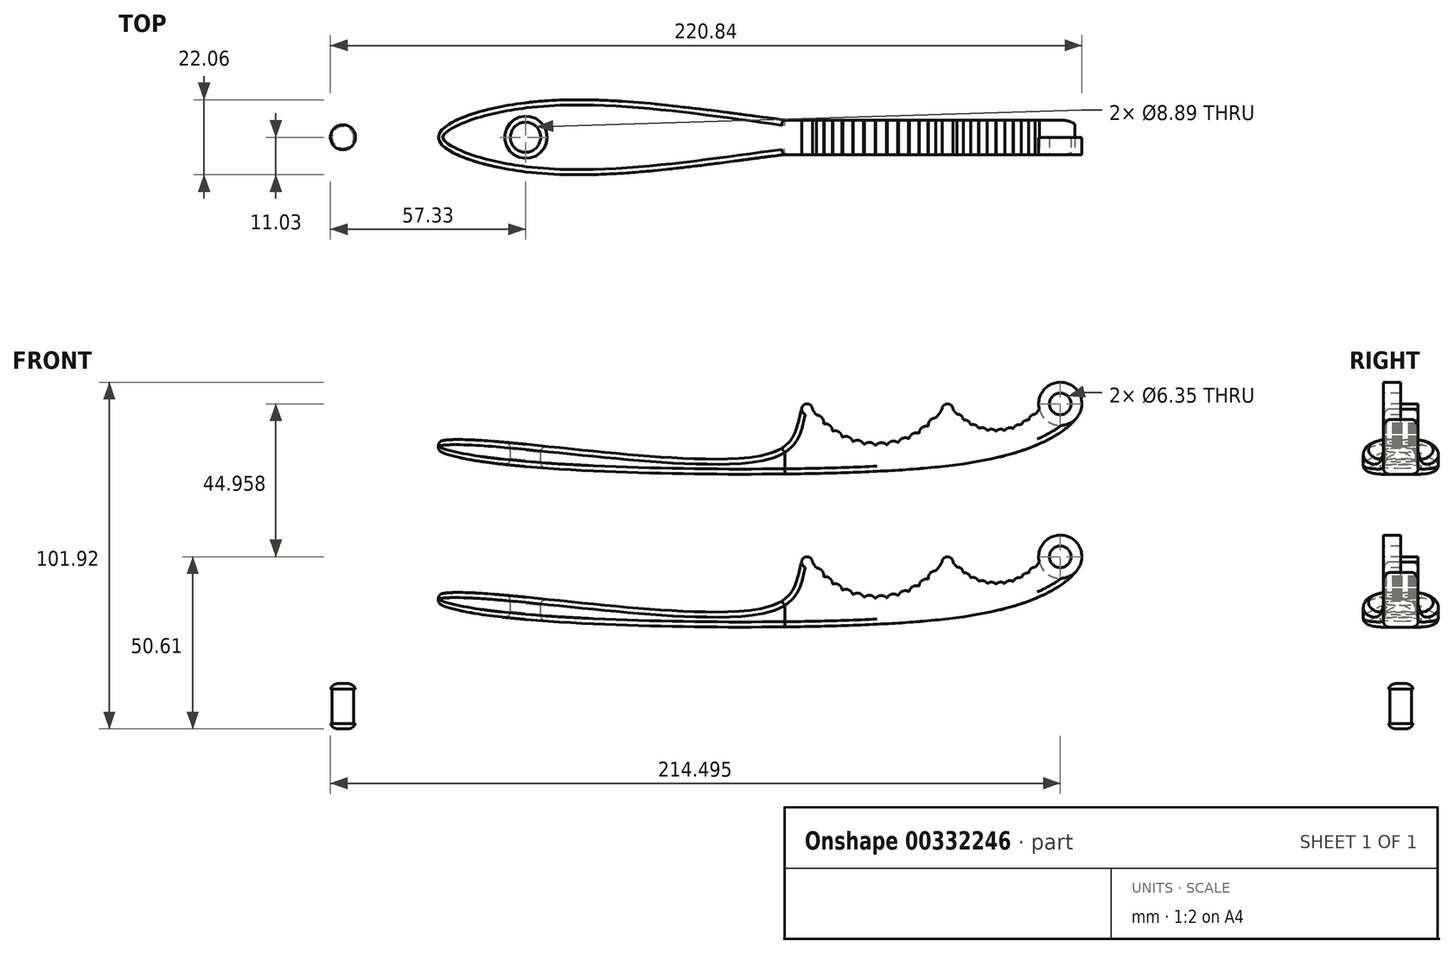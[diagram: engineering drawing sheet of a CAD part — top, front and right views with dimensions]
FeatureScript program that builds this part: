
annotation { "Feature Type Name" : "Feature", "Feature Type Description" : "" }
export const myFeature = defineFeature(function(context is Context, id is Id, definition is map)
    precondition{}
    {
        {
            var Q0;
            Q0=qCreatedBy(makeId("Front.planeOp"),FACE);
            var sketch = newSketch(context, id + "F0", { "sketchPlane" : qUnion([Q0])});
            skLineSegment(sketch, "E0", {"start": v(-75.4, 0) * mm, "end": v(106.36, 0) * mm});
            skCircle(sketch, "E1", {"center": v(106.36, 0) * mm, "radius": 3.18 * mm});
            skCircle(sketch, "E2", {"center": v(106.36, 0) * mm, "radius": 6.35 * mm});
            skLineSegment(sketch, "E3", {"start": v(100.01, 0) * mm, "end": v(77.68, 0) * mm});
            skLineSegment(sketch, "E4", {"start": v(77.68, 0) * mm, "end": v(88.85, 0) * mm});
            skLineSegment(sketch, "E5", {"start": v(-75.4, 0) * mm, "end": v(-75.4, -1.59) * mm});
            skLineSegment(sketch, "E6", {"start": v(106.36, 0) * mm, "end": v(106.36, -1.59) * mm});
            skLineSegment(sketch, "E7", {"start": v(-75.4, -1.59) * mm, "end": v(106.36, -1.59) * mm});
            skArc(sketch, "E8", {"start": v(74.82, -1.59) * mm, "mid": v(73.23, 0) * mm, "end": v(71.64, -1.59) * mm});
            skLineSegment(sketch, "E9", {"start": v(71.64, -1.59) * mm, "end": v(33.54, -1.59) * mm});
            skArc(sketch, "E10", {"start": v(33.54, -1.59) * mm, "mid": v(52.6, -12.22) * mm, "end": v(71.64, -1.59) * mm});
            skArc(sketch, "E11", {"start": v(74.82, -1.59) * mm, "mid": v(87.52, -8.07) * mm, "end": v(100.22, -1.59) * mm});
            skArc(sketch, "E12", {"start": v(33.54, -1.59) * mm, "mid": v(31.95, 0) * mm, "end": v(30.37, -1.59) * mm});
            skLineSegment(sketch, "E13", {"start": v(106.36, 0) * mm, "end": v(112.71, 0) * mm});
            skLineSegment(sketch, "E14", {"start": v(52.6, -12.22) * mm, "end": v(52.6, -19.84) * mm});
            skPoint(sketch, "E15.endSnap0", {"position": v(87.52, -8.07) * mm});
            skLineSegment(sketch, "E16", {"start": v(31.95, -1.59) * mm, "end": v(-76.4, -1.59) * mm});
            skLineSegment(sketch, "E17", {"start": v(106.36, -1.59) * mm, "end": v(106.36, -6.35) * mm});
            skLineSegment(sketch, "E18", {"start": v(106.36, 0) * mm, "end": v(110.68, -4.66) * mm});
            skLineSegment(sketch, "E19", {"start": v(100.22, -1.59) * mm, "end": v(100.22, -11.75) * mm});
            skFitSpline(sketch, "E20", {"points": [v(112.71, 0) * mm, v(110.68, -4.66) * mm, v(100.22, -11.75) * mm, v(52.6, -19.84) * mm, v(-76.4, -13.65) * mm, v(-76.4, -11.11) * mm, v(21.94, -14.29) * mm, v(30.37, -1.59) * mm], "startDerivative": vector(-21.93, -81.83) * mm, "endDerivative": vector(45.44, 125.18) * mm});
            skLineSegment(sketch, "E21", {"start": v(52.6, 10.16) * mm, "end": v(52.6, 10.16) * mm});
            skPoint(sketch, "E22.center", {"position": v(0, 0) * mm});
            skArc(sketch, "E23", {"start": v(69.79, -4.16) * mm, "mid": v(68.16, -4.8) * mm, "end": v(67.59, -6.45) * mm});
            skArc(sketch, "E24.1.0", {"start": v(67.44, -6.58) * mm, "mid": v(65.74, -6.97) * mm, "end": v(64.92, -8.52) * mm});
            skArc(sketch, "E24.2.0", {"start": v(64.76, -8.62) * mm, "mid": v(63.02, -8.75) * mm, "end": v(61.98, -10.16) * mm});
            skArc(sketch, "E24.3.0", {"start": v(61.8, -10.24) * mm, "mid": v(60.06, -10.1) * mm, "end": v(58.82, -11.34) * mm});
            skArc(sketch, "E24.4.0", {"start": v(58.63, -11.4) * mm, "mid": v(56.93, -11) * mm, "end": v(55.52, -12.03) * mm});
            skArc(sketch, "E24.5.0", {"start": v(55.33, -12.05) * mm, "mid": v(53.7, -11.4) * mm, "end": v(52.16, -12.22) * mm});
            skArc(sketch, "E24.6.0", {"start": v(51.96, -12.21) * mm, "mid": v(50.45, -11.33) * mm, "end": v(48.8, -11.9) * mm});
            skArc(sketch, "E24.7.0", {"start": v(48.6, -11.86) * mm, "mid": v(47.25, -10.77) * mm, "end": v(45.53, -11.08) * mm});
            skArc(sketch, "E24.8.0", {"start": v(45.35, -11.02) * mm, "mid": v(44.17, -9.73) * mm, "end": v(42.42, -9.78) * mm});
            skArc(sketch, "E24.9.0", {"start": v(42.25, -9.69) * mm, "mid": v(41.28, -8.24) * mm, "end": v(39.54, -8.02) * mm});
            skArc(sketch, "E24.10.0", {"start": v(39.39, -7.9) * mm, "mid": v(38.64, -6.33) * mm, "end": v(36.96, -5.86) * mm});
            skArc(sketch, "E24.11.0", {"start": v(36.82, -5.72) * mm, "mid": v(36.33, -4.05) * mm, "end": v(34.73, -3.33) * mm});
            skLineSegment(sketch, "E24.anchor1", {"start": v(52.6, 10.16) * mm, "end": v(67.59, -6.45) * mm, "construction": true});
            skLineSegment(sketch, "E24.anchor2", {"start": v(52.6, 10.16) * mm, "end": v(34.73, -3.33) * mm, "construction": true});
            skArc(sketch, "E25", {"start": v(98.99, -3.08) * mm, "mid": v(97.71, -3.56) * mm, "end": v(97.11, -4.79) * mm});
            skArc(sketch, "E26.1.0", {"start": v(97.08, -4.82) * mm, "mid": v(95.74, -5.08) * mm, "end": v(94.95, -6.2) * mm});
            skArc(sketch, "E26.2.0", {"start": v(94.9, -6.22) * mm, "mid": v(93.54, -6.26) * mm, "end": v(92.58, -7.23) * mm});
            skArc(sketch, "E26.3.0", {"start": v(92.54, -7.24) * mm, "mid": v(91.18, -7.06) * mm, "end": v(90.07, -7.86) * mm});
            skArc(sketch, "E26.4.0", {"start": v(90.03, -7.86) * mm, "mid": v(88.73, -7.46) * mm, "end": v(87.5, -8.07) * mm});
            skArc(sketch, "E26.5.0", {"start": v(87.46, -8.07) * mm, "mid": v(86.23, -7.46) * mm, "end": v(84.93, -7.85) * mm});
            skArc(sketch, "E26.6.0", {"start": v(84.88, -7.84) * mm, "mid": v(83.78, -7.04) * mm, "end": v(82.42, -7.22) * mm});
            skArc(sketch, "E26.7.0", {"start": v(82.38, -7.2) * mm, "mid": v(81.42, -6.23) * mm, "end": v(80.06, -6.18) * mm});
            skArc(sketch, "E26.8.0", {"start": v(80.02, -6.16) * mm, "mid": v(79.23, -5.04) * mm, "end": v(77.9, -4.77) * mm});
            skArc(sketch, "E26.9.0", {"start": v(77.86, -4.74) * mm, "mid": v(77.27, -3.51) * mm, "end": v(76, -3.02) * mm});
            skLineSegment(sketch, "E26.anchor1", {"start": v(87.52, 7.62) * mm, "end": v(97.11, -4.79) * mm, "construction": true});
            skLineSegment(sketch, "E26.anchor2", {"start": v(87.52, 7.62) * mm, "end": v(76, -3.02) * mm, "construction": true});
            skLineSegment(sketch, "E27", {"start": v(-76.4, -13.65) * mm, "end": v(-76.4, 0) * mm});
            skLineSegment(sketch, "E28", {"start": v(87.52, 7.62) * mm, "end": v(87.52, 0) * mm});
            skLineSegment(sketch, "E29", {"start": v(52.6, 10.16) * mm, "end": v(52.6, 0) * mm});
            skSolve(sketch);
        }
        {
            var Q0;
            {var subQ15=sQuery(id+"F0.wireOp",EDGE,"E14");Q0=makeQuery(id+"F0.imprint","IMPRINT",FACE,{"disambiguationData":[TD([[makeQuery(id+"F0.imprint","IMPRINT",EDGE,{"derivedFrom":subQ15}),-1.0]])]});}
            var Q1;
            {var subQ3=sQuery(id+"F0.wireOp",EDGE,"E12");var subQ5=makeQuery(id+"F0.imprint","INTERSECT",VERTEX,{"derivedFrom":[sQuery(id+"F0.wireOp",EDGE,"E0"),subQ3]});Q1=makeQuery(id+"F0.imprint","IMPRINT",FACE,{"disambiguationData":[TD([[makeQuery(id+"F0.imprint","IMPRINT",EDGE,{"disambiguationData":[TD([[subQ5,-1.0]])],"derivedFrom":subQ3}),1.0]])]});}
            var Q2;
            {var subQ0=sQuery(id+"F0.wireOp",EDGE,"E24.11.0");Q2=makeQuery(id+"F0.imprint","IMPRINT",FACE,{"disambiguationData":[TD([[makeQuery(id+"F0.imprint","IMPRINT",EDGE,{"derivedFrom":subQ0}),1.0]])]});}
            var Q3;
            {var subQ0=sQuery(id+"F0.wireOp",EDGE,"E24.10.0");Q3=makeQuery(id+"F0.imprint","IMPRINT",FACE,{"disambiguationData":[TD([[makeQuery(id+"F0.imprint","IMPRINT",EDGE,{"derivedFrom":subQ0}),1.0]])]});}
            var Q4;
            {var subQ0=sQuery(id+"F0.wireOp",EDGE,"E24.9.0");Q4=makeQuery(id+"F0.imprint","IMPRINT",FACE,{"disambiguationData":[TD([[makeQuery(id+"F0.imprint","IMPRINT",EDGE,{"derivedFrom":subQ0}),1.0]])]});}
            var Q5;
            {var subQ0=sQuery(id+"F0.wireOp",EDGE,"E24.7.0");Q5=makeQuery(id+"F0.imprint","IMPRINT",FACE,{"disambiguationData":[TD([[makeQuery(id+"F0.imprint","IMPRINT",EDGE,{"derivedFrom":subQ0}),1.0]])]});}
            var Q6;
            {var subQ33=sQuery(id+"F0.wireOp",EDGE,"E14");Q6=makeQuery(id+"F0.imprint","IMPRINT",FACE,{"disambiguationData":[TD([[makeQuery(id+"F0.imprint","IMPRINT",EDGE,{"derivedFrom":subQ33}),1.0]])]});}
            var Q7;
            {var subQ0=sQuery(id+"F0.wireOp",EDGE,"E24.8.0");Q7=makeQuery(id+"F0.imprint","IMPRINT",FACE,{"disambiguationData":[TD([[makeQuery(id+"F0.imprint","IMPRINT",EDGE,{"derivedFrom":subQ0}),1.0]])]});}
            var Q8;
            {var subQ0=sQuery(id+"F0.wireOp",EDGE,"E24.6.0");Q8=makeQuery(id+"F0.imprint","IMPRINT",FACE,{"disambiguationData":[TD([[makeQuery(id+"F0.imprint","IMPRINT",EDGE,{"derivedFrom":subQ0}),1.0]])]});}
            var Q9;
            {var subQ2=sQuery(id+"F0.wireOp",EDGE,"E24.5.0");Q9=makeQuery(id+"F0.imprint","IMPRINT",FACE,{"disambiguationData":[TD([[makeQuery(id+"F0.imprint","IMPRINT",EDGE,{"derivedFrom":subQ2}),1.0]])]});}
            var Q10;
            {var subQ0=sQuery(id+"F0.wireOp",EDGE,"E24.4.0");Q10=makeQuery(id+"F0.imprint","IMPRINT",FACE,{"disambiguationData":[TD([[makeQuery(id+"F0.imprint","IMPRINT",EDGE,{"derivedFrom":subQ0}),1.0]])]});}
            var Q11;
            {var subQ0=sQuery(id+"F0.wireOp",EDGE,"E24.3.0");Q11=makeQuery(id+"F0.imprint","IMPRINT",FACE,{"disambiguationData":[TD([[makeQuery(id+"F0.imprint","IMPRINT",EDGE,{"derivedFrom":subQ0}),1.0]])]});}
            var Q12;
            {var subQ0=sQuery(id+"F0.wireOp",EDGE,"E24.2.0");Q12=makeQuery(id+"F0.imprint","IMPRINT",FACE,{"disambiguationData":[TD([[makeQuery(id+"F0.imprint","IMPRINT",EDGE,{"derivedFrom":subQ0}),1.0]])]});}
            var Q13;
            {var subQ0=sQuery(id+"F0.wireOp",EDGE,"E24.1.0");Q13=makeQuery(id+"F0.imprint","IMPRINT",FACE,{"disambiguationData":[TD([[makeQuery(id+"F0.imprint","IMPRINT",EDGE,{"derivedFrom":subQ0}),1.0]])]});}
            var Q14;
            {var subQ0=sQuery(id+"F0.wireOp",EDGE,"E23");Q14=makeQuery(id+"F0.imprint","IMPRINT",FACE,{"disambiguationData":[TD([[makeQuery(id+"F0.imprint","IMPRINT",EDGE,{"derivedFrom":subQ0}),1.0]])]});}
            var Q15;
            {var subQ0=sQuery(id+"F0.wireOp",EDGE,"E8");var subQ4=makeQuery(id+"F0.imprint","INTERSECT",VERTEX,{"derivedFrom":[sQuery(id+"F0.wireOp",EDGE,"E0"),subQ0]});Q15=makeQuery(id+"F0.imprint","IMPRINT",FACE,{"disambiguationData":[TD([[makeQuery(id+"F0.imprint","IMPRINT",EDGE,{"disambiguationData":[TD([[subQ4,1.0]])],"derivedFrom":subQ0}),1.0]])]});}
            var Q16;
            {var subQ0=sQuery(id+"F0.wireOp",EDGE,"E26.8.0");Q16=makeQuery(id+"F0.imprint","IMPRINT",FACE,{"disambiguationData":[TD([[makeQuery(id+"F0.imprint","IMPRINT",EDGE,{"derivedFrom":subQ0}),1.0]])]});}
            var Q17;
            {var subQ0=sQuery(id+"F0.wireOp",EDGE,"E26.7.0");Q17=makeQuery(id+"F0.imprint","IMPRINT",FACE,{"disambiguationData":[TD([[makeQuery(id+"F0.imprint","IMPRINT",EDGE,{"derivedFrom":subQ0}),1.0]])]});}
            var Q18;
            {var subQ0=sQuery(id+"F0.wireOp",EDGE,"E26.6.0");Q18=makeQuery(id+"F0.imprint","IMPRINT",FACE,{"disambiguationData":[TD([[makeQuery(id+"F0.imprint","IMPRINT",EDGE,{"derivedFrom":subQ0}),1.0]])]});}
            var Q19;
            {var subQ0=sQuery(id+"F0.wireOp",EDGE,"E26.5.0");Q19=makeQuery(id+"F0.imprint","IMPRINT",FACE,{"disambiguationData":[TD([[makeQuery(id+"F0.imprint","IMPRINT",EDGE,{"derivedFrom":subQ0}),1.0]])]});}
            var Q20;
            {var subQ0=sQuery(id+"F0.wireOp",EDGE,"E26.4.0");Q20=makeQuery(id+"F0.imprint","IMPRINT",FACE,{"disambiguationData":[TD([[makeQuery(id+"F0.imprint","IMPRINT",EDGE,{"derivedFrom":subQ0}),1.0]])]});}
            var Q21;
            {var subQ0=sQuery(id+"F0.wireOp",EDGE,"E26.3.0");Q21=makeQuery(id+"F0.imprint","IMPRINT",FACE,{"disambiguationData":[TD([[makeQuery(id+"F0.imprint","IMPRINT",EDGE,{"derivedFrom":subQ0}),1.0]])]});}
            var Q22;
            {var subQ0=sQuery(id+"F0.wireOp",EDGE,"E26.2.0");Q22=makeQuery(id+"F0.imprint","IMPRINT",FACE,{"disambiguationData":[TD([[makeQuery(id+"F0.imprint","IMPRINT",EDGE,{"derivedFrom":subQ0}),1.0]])]});}
            var Q23;
            {var subQ0=sQuery(id+"F0.wireOp",EDGE,"E26.1.0");Q23=makeQuery(id+"F0.imprint","IMPRINT",FACE,{"disambiguationData":[TD([[makeQuery(id+"F0.imprint","IMPRINT",EDGE,{"derivedFrom":subQ0}),1.0]])]});}
            var Q24;
            {var subQ0=sQuery(id+"F0.wireOp",EDGE,"E25");Q24=makeQuery(id+"F0.imprint","IMPRINT",FACE,{"disambiguationData":[TD([[makeQuery(id+"F0.imprint","IMPRINT",EDGE,{"derivedFrom":subQ0}),1.0]])]});}
            var Q25;
            {var subQ0=sQuery(id+"F0.wireOp",EDGE,"E26.9.0");Q25=makeQuery(id+"F0.imprint","IMPRINT",FACE,{"disambiguationData":[TD([[makeQuery(id+"F0.imprint","IMPRINT",EDGE,{"derivedFrom":subQ0}),1.0]])]});}
            var Q26;
            {var subQ1=sQuery(id+"F0.wireOp",EDGE,"E0");var subQ3=sQuery(id+"F0.wireOp",EDGE,"E1");var subQ4=makeQuery(id+"F0.imprint","INTERSECT",VERTEX,{"derivedFrom":[subQ1,subQ3]});Q26=makeQuery(id+"F0.imprint","IMPRINT",FACE,{"disambiguationData":[TD([[makeQuery(id+"F0.imprint","IMPRINT",EDGE,{"disambiguationData":[TD([[subQ4,1.0]])],"derivedFrom":subQ3}),-1.0]])]});}
            var Q27;
            {var subQ1=sQuery(id+"F0.wireOp",EDGE,"E0");var subQ3=sQuery(id+"F0.wireOp",EDGE,"E1");var subQ4=makeQuery(id+"F0.imprint","INTERSECT",VERTEX,{"derivedFrom":[subQ1,subQ3]});Q27=makeQuery(id+"F0.imprint","IMPRINT",FACE,{"disambiguationData":[TD([[makeQuery(id+"F0.imprint","IMPRINT",EDGE,{"disambiguationData":[TD([[subQ4,1.0]])],"derivedFrom":subQ3}),1.0]])]});}
            var Q28;
            {var subQ0=sQuery(id+"F0.wireOp",EDGE,"E13");var subQ1=sQuery(id+"F0.wireOp",EDGE,"E1");var subQ2=makeQuery(id+"F0.imprint","INTERSECT",VERTEX,{"derivedFrom":[subQ1,subQ0]});Q28=makeQuery(id+"F0.imprint","IMPRINT",FACE,{"disambiguationData":[TD([[makeQuery(id+"F0.imprint","IMPRINT",EDGE,{"disambiguationData":[TD([[subQ2,1.0]])],"derivedFrom":subQ1}),-1.0]])]});}
            var Q29;
            {var subQ0=sQuery(id+"F0.wireOp",EDGE,"E17");var subQ1=sQuery(id+"F0.wireOp",EDGE,"E1");var subQ2=makeQuery(id+"F0.imprint","INTERSECT",VERTEX,{"derivedFrom":[subQ1,subQ0]});Q29=makeQuery(id+"F0.imprint","IMPRINT",FACE,{"disambiguationData":[TD([[makeQuery(id+"F0.imprint","IMPRINT",EDGE,{"disambiguationData":[TD([[subQ2,-1.0]])],"derivedFrom":subQ1}),-1.0]])]});}
            var Q30;
            {var subQ0=sQuery(id+"F0.wireOp",EDGE,"E7");var subQ1=sQuery(id+"F0.wireOp",EDGE,"E1");var subQ2=makeQuery(id+"F0.imprint","INTERSECT",VERTEX,{"derivedFrom":[subQ1,subQ0]});Q30=makeQuery(id+"F0.imprint","IMPRINT",FACE,{"disambiguationData":[TD([[makeQuery(id+"F0.imprint","IMPRINT",EDGE,{"disambiguationData":[TD([[subQ2,-1.0]])],"derivedFrom":subQ1}),-1.0]])]});}
            var Q31;
            {var subQ1=sQuery(id+"F0.wireOp",EDGE,"E0");var subQ3=sQuery(id+"F0.wireOp",EDGE,"E1");var subQ4=makeQuery(id+"F0.imprint","INTERSECT",VERTEX,{"derivedFrom":[subQ1,subQ3]});Q31=makeQuery(id+"F0.imprint","IMPRINT",FACE,{"disambiguationData":[TD([[makeQuery(id+"F0.imprint","IMPRINT",EDGE,{"disambiguationData":[TD([[subQ4,-1.0]])],"derivedFrom":subQ3}),-1.0]])]});}
            var Q32;
            {var subQ0=sQuery(id+"F0.wireOp",EDGE,"E19");Q32=makeQuery(id+"F0.imprint","IMPRINT",FACE,{"disambiguationData":[TD([[makeQuery(id+"F0.imprint","IMPRINT",EDGE,{"derivedFrom":subQ0}),1.0]])]});}
            var Q33;
            {var subQ0=sQuery(id+"F0.wireOp",EDGE,"E13");var subQ1=sQuery(id+"F0.wireOp",EDGE,"E1");var subQ2=makeQuery(id+"F0.imprint","INTERSECT",VERTEX,{"derivedFrom":[subQ1,subQ0]});Q33=makeQuery(id+"F0.imprint","IMPRINT",FACE,{"disambiguationData":[TD([[makeQuery(id+"F0.imprint","IMPRINT",EDGE,{"disambiguationData":[TD([[subQ2,1.0]])],"derivedFrom":subQ1}),1.0]])]});}
            var Q34;
            {var subQ5=sQuery(id+"F0.wireOp",EDGE,"E6");Q34=makeQuery(id+"F0.imprint","IMPRINT",FACE,{"disambiguationData":[TD([[makeQuery(id+"F0.imprint","IMPRINT",EDGE,{"derivedFrom":subQ5}),1.0]])]});}
            var Q35;
            {var subQ0=sQuery(id+"F0.wireOp",EDGE,"E7");var subQ1=sQuery(id+"F0.wireOp",EDGE,"E1");var subQ2=makeQuery(id+"F0.imprint","INTERSECT",VERTEX,{"derivedFrom":[subQ1,subQ0]});Q35=makeQuery(id+"F0.imprint","IMPRINT",FACE,{"disambiguationData":[TD([[makeQuery(id+"F0.imprint","IMPRINT",EDGE,{"disambiguationData":[TD([[subQ2,-1.0]])],"derivedFrom":subQ1}),1.0]])]});}
            var Q36;
            {var subQ0=sQuery(id+"F0.wireOp",EDGE,"E6");Q36=makeQuery(id+"F0.imprint","IMPRINT",FACE,{"disambiguationData":[TD([[makeQuery(id+"F0.imprint","IMPRINT",EDGE,{"derivedFrom":subQ0}),-1.0]])]});}
            var Q37;
            {var subQ0=sQuery(id+"F0.wireOp",EDGE,"E20");var subQ1=sQuery(id+"F0.wireOp",EDGE,"E2");var subQ2=makeQuery(id+"F0.imprint","INTERSECT",VERTEX,{"derivedFrom":[subQ1,sQuery(id+"F0.wireOp",EDGE,"E13"),subQ0]});Q37=makeQuery(id+"F0.imprint","IMPRINT",FACE,{"disambiguationData":[TD([[makeQuery(id+"F0.imprint","IMPRINT",EDGE,{"disambiguationData":[TD([[subQ2,1.0]])],"derivedFrom":subQ1}),1.0]])]});}
            extrude(context, id + "F1", {"entities" : qUnion([Q0, Q1, Q2, Q3, Q4, Q5, Q6, Q7, Q8, Q9, Q10, Q11, Q12, Q13, Q14, Q15, Q16, Q17, Q18, Q19, Q20, Q21, Q22, Q23, Q24, Q25, Q26, Q27, Q28, Q29, Q30, Q31, Q32, Q33, Q34, Q35, Q36, Q37]), "endBound" : BoundingType.SYMMETRIC, "oppositeDirection" : true, "depth" : 50.8 * mm});
        }
        {
            var Q0;
            Q0=qCreatedBy(makeId("Top.planeOp"),FACE);
            var sketch = newSketch(context, id + "F2", { "sketchPlane" : qUnion([Q0])});
            skLineSegment(sketch, "E30", {"start": v(0, 0) * mm, "end": v(0, 5.08) * mm});
            skLineSegment(sketch, "E31", {"start": v(0, 0) * mm, "end": v(-76.4, 0) * mm});
            skLineSegment(sketch, "E32", {"start": v(-76.4, 0) * mm, "end": v(-50.8, 0) * mm});
            skLineSegment(sketch, "E33", {"start": v(-50.8, 0) * mm, "end": v(-50.8, 10.16) * mm});
            skLineSegment(sketch, "E34", {"start": v(-50.8, 0) * mm, "end": v(-50.8, -10.16) * mm});
            skFitSpline(sketch, "E35", {"points": [v(25.4, 5.08) * mm, v(-50.8, 10.16) * mm, v(-76.4, 0) * mm, v(-50.8, -10.16) * mm, v(25.4, -5.08) * mm], "startDerivative": vector(-261.64, 33.06) * mm, "endDerivative": vector(261.64, 33.06) * mm});
            skLineSegment(sketch, "E36.bottom", {"start": v(-95.72, 47.14) * mm, "end": v(121.7, 47.14) * mm});
            skLineSegment(sketch, "E36.top", {"start": v(-95.72, -31.52) * mm, "end": v(121.7, -31.52) * mm});
            skLineSegment(sketch, "E36.left", {"start": v(-95.72, 47.14) * mm, "end": v(-95.72, -31.52) * mm});
            skLineSegment(sketch, "E36.right", {"start": v(121.7, 47.14) * mm, "end": v(121.7, -31.52) * mm});
            skLineSegment(sketch, "E37.bottom", {"start": v(0, 5.08) * mm, "end": v(142.43, 5.08) * mm});
            skLineSegment(sketch, "E37.top", {"start": v(0, -5.08) * mm, "end": v(142.43, -5.08) * mm});
            skLineSegment(sketch, "E37.left", {"start": v(0, 5.08) * mm, "end": v(0, -5.08) * mm});
            skLineSegment(sketch, "E37.right", {"start": v(142.43, 5.08) * mm, "end": v(142.43, -5.08) * mm});
            skCircle(sketch, "E38", {"center": v(-50.8, 0) * mm, "radius": 4.45 * mm});
            skSolve(sketch);
        }
        {
            var Q0;
            {var subQ4=sQuery(id+"F2.wireOp",EDGE,"E36.bottom");Q0=makeQuery(id+"F2.imprint","IMPRINT",FACE,{"disambiguationData":[TD([[makeQuery(id+"F2.imprint","IMPRINT",EDGE,{"derivedFrom":subQ4}),-1.0]])]});}
            var Q1;
            {var subQ1=sQuery(id+"F2.wireOp",EDGE,"E31");var subQ3=sQuery(id+"F2.wireOp",EDGE,"E38");var subQ4=makeQuery(id+"F2.imprint","INTERSECT",VERTEX,{"derivedFrom":[subQ1,subQ3]});Q1=makeQuery(id+"F2.imprint","IMPRINT",FACE,{"disambiguationData":[TD([[makeQuery(id+"F2.imprint","IMPRINT",EDGE,{"disambiguationData":[TD([[subQ4,1.0]])],"derivedFrom":subQ3}),1.0]])]});}
            var Q2;
            {var subQ1=sQuery(id+"F2.wireOp",EDGE,"E32");var subQ3=sQuery(id+"F2.wireOp",EDGE,"E38");var subQ4=makeQuery(id+"F2.imprint","INTERSECT",VERTEX,{"derivedFrom":[subQ1,subQ3]});Q2=makeQuery(id+"F2.imprint","IMPRINT",FACE,{"disambiguationData":[TD([[makeQuery(id+"F2.imprint","IMPRINT",EDGE,{"disambiguationData":[TD([[subQ4,-1.0]])],"derivedFrom":subQ3}),1.0]])]});}
            var Q3;
            {var subQ1=sQuery(id+"F2.wireOp",EDGE,"E32");var subQ3=sQuery(id+"F2.wireOp",EDGE,"E38");var subQ4=makeQuery(id+"F2.imprint","INTERSECT",VERTEX,{"derivedFrom":[subQ1,subQ3]});Q3=makeQuery(id+"F2.imprint","IMPRINT",FACE,{"disambiguationData":[TD([[makeQuery(id+"F2.imprint","IMPRINT",EDGE,{"disambiguationData":[TD([[subQ4,1.0]])],"derivedFrom":subQ3}),1.0]])]});}
            var Q4;
            {var subQ1=sQuery(id+"F2.wireOp",EDGE,"E31");var subQ3=sQuery(id+"F2.wireOp",EDGE,"E38");var subQ4=makeQuery(id+"F2.imprint","INTERSECT",VERTEX,{"derivedFrom":[subQ1,subQ3]});Q4=makeQuery(id+"F2.imprint","IMPRINT",FACE,{"disambiguationData":[TD([[makeQuery(id+"F2.imprint","IMPRINT",EDGE,{"disambiguationData":[TD([[subQ4,-1.0]])],"derivedFrom":subQ3}),1.0]])]});}
            extrude(context, id + "F3", {"entities" : qUnion([Q0, Q1, Q2, Q3, Q4]), "operationType" : NewBodyOperationType.REMOVE, "endBound" : BoundingType.SYMMETRIC, "oppositeDirection" : true, "depth" : 50.8 * mm});
        }
        {
            var Q0;
            {var subQ0=sQuery(id+"F0.wireOp",EDGE,"E7");var subQ1=sQuery(id+"F0.wireOp",EDGE,"E1");var subQ2=makeQuery(id+"F0.imprint","INTERSECT",VERTEX,{"derivedFrom":[subQ1,subQ0]});Q0=makeQuery(id+"F0.imprint","IMPRINT",FACE,{"disambiguationData":[TD([[makeQuery(id+"F0.imprint","IMPRINT",EDGE,{"disambiguationData":[TD([[subQ2,-1.0]])],"derivedFrom":subQ1}),1.0]])]});}
            var Q1;
            {var subQ0=sQuery(id+"F0.wireOp",EDGE,"E6");Q1=makeQuery(id+"F0.imprint","IMPRINT",FACE,{"disambiguationData":[TD([[makeQuery(id+"F0.imprint","IMPRINT",EDGE,{"derivedFrom":subQ0}),-1.0]])]});}
            var Q2;
            {var subQ5=sQuery(id+"F0.wireOp",EDGE,"E6");Q2=makeQuery(id+"F0.imprint","IMPRINT",FACE,{"disambiguationData":[TD([[makeQuery(id+"F0.imprint","IMPRINT",EDGE,{"derivedFrom":subQ5}),1.0]])]});}
            var Q3;
            {var subQ0=sQuery(id+"F0.wireOp",EDGE,"E13");var subQ1=sQuery(id+"F0.wireOp",EDGE,"E1");var subQ2=makeQuery(id+"F0.imprint","INTERSECT",VERTEX,{"derivedFrom":[subQ1,subQ0]});Q3=makeQuery(id+"F0.imprint","IMPRINT",FACE,{"disambiguationData":[TD([[makeQuery(id+"F0.imprint","IMPRINT",EDGE,{"disambiguationData":[TD([[subQ2,1.0]])],"derivedFrom":subQ1}),1.0]])]});}
            var Q4;
            {var subQ1=sQuery(id+"F0.wireOp",EDGE,"E0");var subQ3=sQuery(id+"F0.wireOp",EDGE,"E1");var subQ4=makeQuery(id+"F0.imprint","INTERSECT",VERTEX,{"derivedFrom":[subQ1,subQ3]});Q4=makeQuery(id+"F0.imprint","IMPRINT",FACE,{"disambiguationData":[TD([[makeQuery(id+"F0.imprint","IMPRINT",EDGE,{"disambiguationData":[TD([[subQ4,1.0]])],"derivedFrom":subQ3}),1.0]])]});}
            extrude(context, id + "F4", {"entities" : qUnion([Q0, Q1, Q2, Q3, Q4]), "operationType" : NewBodyOperationType.REMOVE, "endBound" : BoundingType.SYMMETRIC, "oppositeDirection" : true, "depth" : 50.8 * mm});
        }
        {
            var Q0;
            {var subQ0=sQuery(id+"F0.wireOp",EDGE,"E7");var subQ1=sQuery(id+"F0.wireOp",EDGE,"E1");var subQ2=makeQuery(id+"F0.imprint","INTERSECT",VERTEX,{"derivedFrom":[subQ1,subQ0]});Q0=makeQuery(id+"F0.imprint","IMPRINT",FACE,{"disambiguationData":[TD([[makeQuery(id+"F0.imprint","IMPRINT",EDGE,{"disambiguationData":[TD([[subQ2,-1.0]])],"derivedFrom":subQ1}),-1.0]])]});}
            var Q1;
            {var subQ1=sQuery(id+"F0.wireOp",EDGE,"E0");var subQ3=sQuery(id+"F0.wireOp",EDGE,"E1");var subQ4=makeQuery(id+"F0.imprint","INTERSECT",VERTEX,{"derivedFrom":[subQ1,subQ3]});Q1=makeQuery(id+"F0.imprint","IMPRINT",FACE,{"disambiguationData":[TD([[makeQuery(id+"F0.imprint","IMPRINT",EDGE,{"disambiguationData":[TD([[subQ4,1.0]])],"derivedFrom":subQ3}),-1.0]])]});}
            var Q2;
            {var subQ1=sQuery(id+"F0.wireOp",EDGE,"E0");var subQ3=sQuery(id+"F0.wireOp",EDGE,"E1");var subQ4=makeQuery(id+"F0.imprint","INTERSECT",VERTEX,{"derivedFrom":[subQ1,subQ3]});Q2=makeQuery(id+"F0.imprint","IMPRINT",FACE,{"disambiguationData":[TD([[makeQuery(id+"F0.imprint","IMPRINT",EDGE,{"disambiguationData":[TD([[subQ4,-1.0]])],"derivedFrom":subQ3}),-1.0]])]});}
            var Q3;
            {var subQ0=sQuery(id+"F0.wireOp",EDGE,"E13");var subQ1=sQuery(id+"F0.wireOp",EDGE,"E1");var subQ2=makeQuery(id+"F0.imprint","INTERSECT",VERTEX,{"derivedFrom":[subQ1,subQ0]});Q3=makeQuery(id+"F0.imprint","IMPRINT",FACE,{"disambiguationData":[TD([[makeQuery(id+"F0.imprint","IMPRINT",EDGE,{"disambiguationData":[TD([[subQ2,1.0]])],"derivedFrom":subQ1}),-1.0]])]});}
            var Q4;
            {var subQ0=sQuery(id+"F0.wireOp",EDGE,"E17");var subQ1=sQuery(id+"F0.wireOp",EDGE,"E1");var subQ2=makeQuery(id+"F0.imprint","INTERSECT",VERTEX,{"derivedFrom":[subQ1,subQ0]});Q4=makeQuery(id+"F0.imprint","IMPRINT",FACE,{"disambiguationData":[TD([[makeQuery(id+"F0.imprint","IMPRINT",EDGE,{"disambiguationData":[TD([[subQ2,-1.0]])],"derivedFrom":subQ1}),-1.0]])]});}
            var Q5;
            {var subQ0=sQuery(id+"F0.wireOp",EDGE,"E20");var subQ1=sQuery(id+"F0.wireOp",EDGE,"E2");var subQ2=makeQuery(id+"F0.imprint","INTERSECT",VERTEX,{"derivedFrom":[subQ1,sQuery(id+"F0.wireOp",EDGE,"E13"),subQ0]});Q5=makeQuery(id+"F0.imprint","IMPRINT",FACE,{"disambiguationData":[TD([[makeQuery(id+"F0.imprint","IMPRINT",EDGE,{"disambiguationData":[TD([[subQ2,1.0]])],"derivedFrom":subQ1}),1.0]])]});}
            extrude(context, id + "F5", {"entities" : qUnion([Q0, Q1, Q2, Q3, Q4, Q5]), "operationType" : NewBodyOperationType.REMOVE, "oppositeDirection" : true, "depth" : 25.4 * mm});
        }
        {
            var Q0;
            Q0=makeQuery(id+"F3.boolean.opBoolean","INTERSECT",EDGE,{"disambiguationData":[OD(1.0)],"derivedFrom":[makeQuery(id+"F1.opExtrude","SWEPT_FACE",FACE,{"disambiguationData":[OSD([sQuery(id+"F0.wireOp",EDGE,"E20")])]}),makeQuery(id+"F3.opExtrude","SWEPT_FACE",FACE,{"disambiguationData":[OSD([sQuery(id+"F2.wireOp",EDGE,"E37.top")])]})]});
            var Q1;
            Q1=makeQuery(id+"F3.boolean.opBoolean","INTERSECT",EDGE,{"disambiguationData":[OD(1.0)],"derivedFrom":[makeQuery(id+"F1.opExtrude","SWEPT_FACE",FACE,{"disambiguationData":[OSD([sQuery(id+"F0.wireOp",EDGE,"E20")])]}),makeQuery(id+"F3.opExtrude","SWEPT_FACE",FACE,{"disambiguationData":[OSD([sQuery(id+"F2.wireOp",EDGE,"E37.bottom")])]})]});
            var Q2;
            Q2=makeQuery(id+"F3.boolean.opBoolean","INTERSECT",EDGE,{"disambiguationData":[OD(1.0)],"derivedFrom":[makeQuery(id+"F1.opExtrude","SWEPT_FACE",FACE,{"disambiguationData":[OSD([sQuery(id+"F0.wireOp",EDGE,"E20")])]}),makeQuery(id+"F3.opExtrude","SWEPT_FACE",FACE,{"disambiguationData":[OSD([sQuery(id+"F2.wireOp",EDGE,"E35")])]})]});
            var Q3;
            Q3=makeQuery(id+"F3.boolean.opBoolean","INTERSECT",EDGE,{"disambiguationData":[OD(0.0)],"derivedFrom":[makeQuery(id+"F1.opExtrude","SWEPT_FACE",FACE,{"disambiguationData":[OSD([sQuery(id+"F0.wireOp",EDGE,"E20")])]}),makeQuery(id+"F3.opExtrude","SWEPT_FACE",FACE,{"disambiguationData":[OSD([sQuery(id+"F2.wireOp",EDGE,"E35")])]})]});
            var Q4;
            Q4=makeQuery(id+"F3.boolean.opBoolean","INTERSECT",EDGE,{"disambiguationData":[OD(0.0)],"derivedFrom":[makeQuery(id+"F1.opExtrude","SWEPT_FACE",FACE,{"disambiguationData":[OSD([sQuery(id+"F0.wireOp",EDGE,"E20")])]}),makeQuery(id+"F3.opExtrude","SWEPT_FACE",FACE,{"disambiguationData":[OSD([sQuery(id+"F2.wireOp",EDGE,"E37.top")])]})]});
            var Q5;
            Q5=makeQuery(id+"F3.boolean.opBoolean","INTERSECT",EDGE,{"disambiguationData":[OD(0.0)],"derivedFrom":[makeQuery(id+"F1.opExtrude","SWEPT_FACE",FACE,{"disambiguationData":[OSD([sQuery(id+"F0.wireOp",EDGE,"E20")])]}),makeQuery(id+"F3.opExtrude","SWEPT_FACE",FACE,{"disambiguationData":[OSD([sQuery(id+"F2.wireOp",EDGE,"E37.bottom")])]})]});
            fillet(context, id + "F6", {"entities" : qUnion([Q0, Q1, Q2, Q3, Q4, Q5]), "radius" : 1.52 * mm, "tangentPropagation" : true, "allowEdgeOverflow" : false});
        }
        {
            var Q0;
            Q0=makeQuery(id+"F3.boolean.opBoolean","INTERSECT",EDGE,{"disambiguationData":[OD(0.0)],"derivedFrom":[makeQuery(id+"F1.opExtrude","SWEPT_FACE",FACE,{"disambiguationData":[OSD([sQuery(id+"F0.wireOp",EDGE,"E20")])]}),makeQuery(id+"F3.opExtrude","SWEPT_FACE",FACE,{"disambiguationData":[OSD([sQuery(id+"F2.wireOp",EDGE,"E38")])]})]});
            var Q1;
            Q1=makeQuery(id+"F3.boolean.opBoolean","INTERSECT",EDGE,{"disambiguationData":[OD(1.0)],"derivedFrom":[makeQuery(id+"F1.opExtrude","SWEPT_FACE",FACE,{"disambiguationData":[OSD([sQuery(id+"F0.wireOp",EDGE,"E20")])]}),makeQuery(id+"F3.opExtrude","SWEPT_FACE",FACE,{"disambiguationData":[OSD([sQuery(id+"F2.wireOp",EDGE,"E38")])]})]});
            fillet(context, id + "F7", {"entities" : qUnion([Q0, Q1]), "radius" : 1.78 * mm, "tangentPropagation" : true, "allowEdgeOverflow" : false});
        }
        {
            var Q0;
            Q0=makeQuery(id+"F1.opExtrude","SWEPT_BODY",BODY,{"disambiguationData":[OSD([sQuery(id+"F0.wireOp",EDGE,"E2"),sQuery(id+"F0.wireOp",EDGE,"E8"),sQuery(id+"F0.wireOp",EDGE,"E10"),sQuery(id+"F0.wireOp",EDGE,"E11"),sQuery(id+"F0.wireOp",EDGE,"E12"),sQuery(id+"F0.wireOp",EDGE,"E20"),sQuery(id+"F0.wireOp",EDGE,"E23"),sQuery(id+"F0.wireOp",EDGE,"E24.1.0"),sQuery(id+"F0.wireOp",EDGE,"E24.2.0"),sQuery(id+"F0.wireOp",EDGE,"E24.3.0"),sQuery(id+"F0.wireOp",EDGE,"E24.4.0"),sQuery(id+"F0.wireOp",EDGE,"E24.5.0"),sQuery(id+"F0.wireOp",EDGE,"E24.6.0"),sQuery(id+"F0.wireOp",EDGE,"E24.7.0"),sQuery(id+"F0.wireOp",EDGE,"E24.8.0"),sQuery(id+"F0.wireOp",EDGE,"E24.9.0"),sQuery(id+"F0.wireOp",EDGE,"E24.10.0"),sQuery(id+"F0.wireOp",EDGE,"E24.11.0"),sQuery(id+"F0.wireOp",EDGE,"E25"),sQuery(id+"F0.wireOp",EDGE,"E26.1.0"),sQuery(id+"F0.wireOp",EDGE,"E26.2.0"),sQuery(id+"F0.wireOp",EDGE,"E26.3.0"),sQuery(id+"F0.wireOp",EDGE,"E26.4.0"),sQuery(id+"F0.wireOp",EDGE,"E26.5.0"),sQuery(id+"F0.wireOp",EDGE,"E26.6.0"),sQuery(id+"F0.wireOp",EDGE,"E26.7.0"),sQuery(id+"F0.wireOp",EDGE,"E26.8.0"),sQuery(id+"F0.wireOp",EDGE,"E26.9.0")])]});
            transform(context, id + "F8", {"entities" : qUnion([Q0]), "transformType" : TransformType.TRANSLATION_3D, "dx" : 0 * mm, "dy" : 0 * mm, "dz" : 44.96 * mm, "makeCopy" : true});
        }
        {
            var Q0;
            Q0=qCreatedBy(makeId("Front.planeOp"),FACE);
            var sketch = newSketch(context, id + "F9", { "sketchPlane" : qUnion([Q0])});
            skLineSegment(sketch, "E39", {"start": v(-104.45, -38.87) * mm, "end": v(-104.45, -49.03) * mm});
            skLineSegment(sketch, "E40", {"start": v(-104.45, -38.87) * mm, "end": v(-101.28, -38.87) * mm});
            skLineSegment(sketch, "E41", {"start": v(-104.45, -49.03) * mm, "end": v(-101.28, -49.03) * mm});
            skLineSegment(sketch, "E42", {"start": v(-104.45, -38.87) * mm, "end": v(-104.45, -37.28) * mm});
            skLineSegment(sketch, "E43", {"start": v(-104.45, -37.28) * mm, "end": v(-100.77, -37.28) * mm});
            skLineSegment(sketch, "E44", {"start": v(-100.77, -37.28) * mm, "end": v(-100.77, -38.87) * mm});
            skLineSegment(sketch, "E45", {"start": v(-100.77, -38.87) * mm, "end": v(-101.28, -38.87) * mm});
            skLineSegment(sketch, "E46", {"start": v(-101.28, -38.87) * mm, "end": v(-101.28, -49.03) * mm});
            skLineSegment(sketch, "E47", {"start": v(-104.45, -49.03) * mm, "end": v(-104.45, -50.61) * mm});
            skLineSegment(sketch, "E48", {"start": v(-104.45, -50.61) * mm, "end": v(-100.77, -50.61) * mm});
            skLineSegment(sketch, "E49", {"start": v(-100.77, -50.61) * mm, "end": v(-100.77, -49.03) * mm});
            skLineSegment(sketch, "E50", {"start": v(-100.77, -49.03) * mm, "end": v(-101.28, -49.03) * mm});
            skSolve(sketch);
        }
        {
            var Q0;
            Q0=makeQuery(id+"F9.imprint","IMPRINT",FACE,{"disambiguationData":[TD([[makeQuery(id+"F9.imprint","IMPRINT",EDGE,{"derivedFrom":sQuery(id+"F9.wireOp",EDGE,"E39")}),1.0]])]});
            var Q1;
            Q1=makeQuery(id+"F9.imprint","IMPRINT",FACE,{"disambiguationData":[TD([[makeQuery(id+"F9.imprint","IMPRINT",EDGE,{"derivedFrom":sQuery(id+"F9.wireOp",EDGE,"E41")}),-1.0]])]});
            var Q2;
            Q2=makeQuery(id+"F9.imprint","IMPRINT",FACE,{"disambiguationData":[TD([[makeQuery(id+"F9.imprint","IMPRINT",EDGE,{"derivedFrom":sQuery(id+"F9.wireOp",EDGE,"E40")}),1.0]])]});
            var Q3;
            Q3=sQuery(id+"F9.wireOp",EDGE,"E39");
            revolve(context, id + "F10", {"entities" : qUnion([Q0, Q1, Q2]), "axis" : qUnion([Q3]), "revolveType" : RevolveType.FULL});
        }
        {
            var Q0;
            Q0=makeQuery(id+"F10.opRevolve","SWEPT_EDGE",EDGE,{"disambiguationData":[OSD([sQuery(id+"F9.wireOp",EDGE,"E43"),sQuery(id+"F9.wireOp",EDGE,"E44")])]});
            var Q1;
            Q1=makeQuery(id+"F10.opRevolve","SWEPT_EDGE",EDGE,{"disambiguationData":[OSD([sQuery(id+"F9.wireOp",EDGE,"E48"),sQuery(id+"F9.wireOp",EDGE,"E49")])]});
            fillet(context, id + "F11", {"entities" : qUnion([Q0, Q1]), "radius" : 2.54 * mm, "tangentPropagation" : true, "allowEdgeOverflow" : false});
        }
    });
